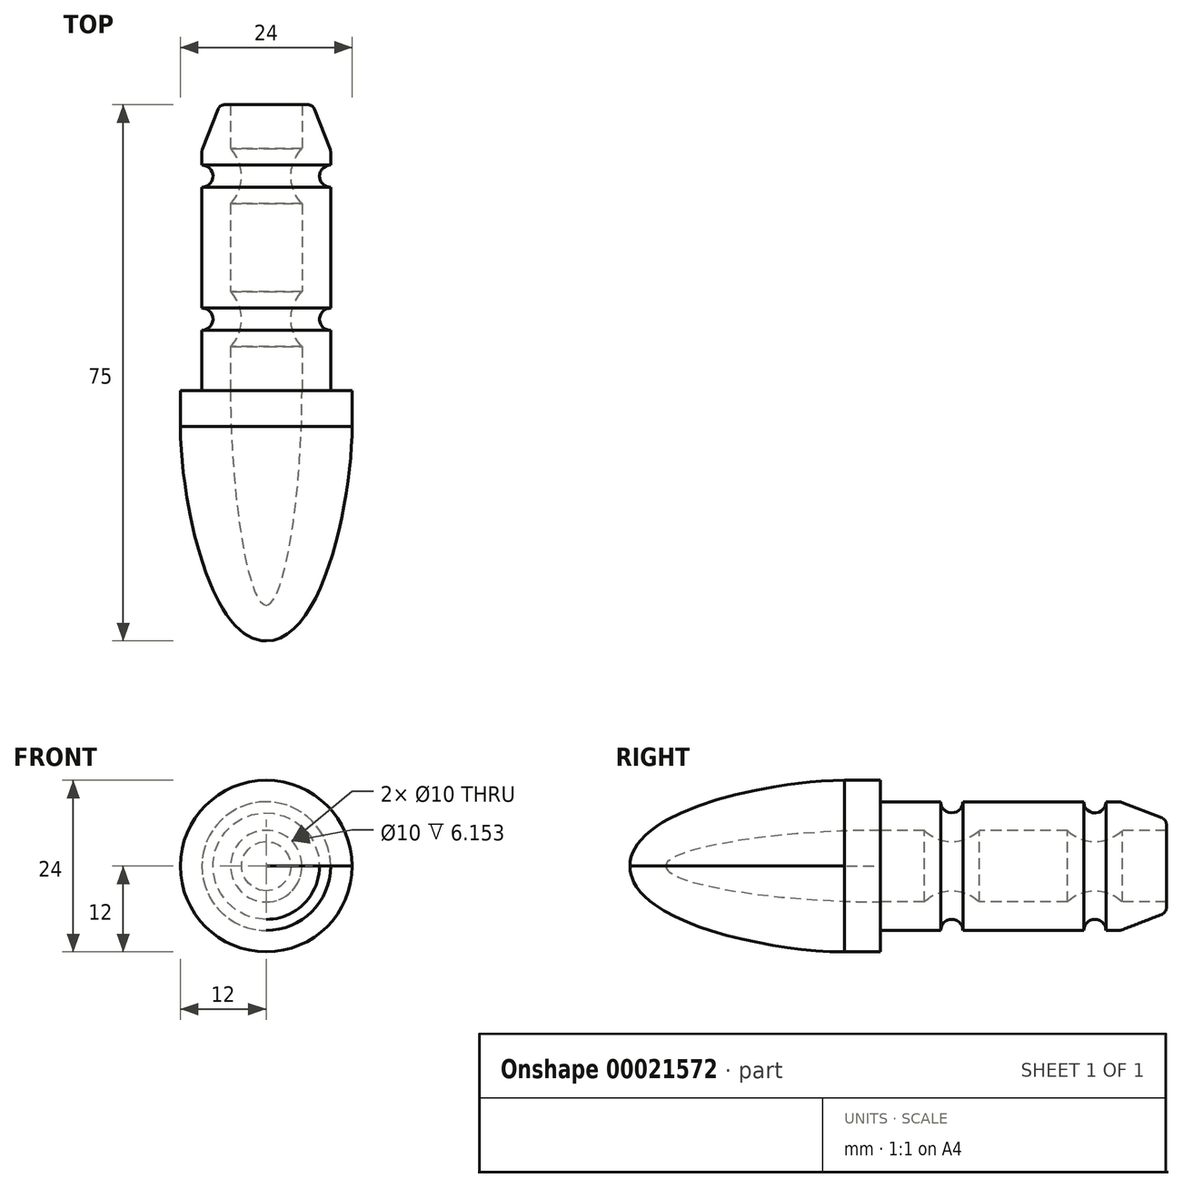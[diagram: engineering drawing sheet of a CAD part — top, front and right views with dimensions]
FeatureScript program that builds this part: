
annotation { "Feature Type Name" : "Feature", "Feature Type Description" : "" }
export const myFeature = defineFeature(function(context is Context, id is Id, definition is map)
    precondition{}
    {
        {
            var Q0;
            Q0=qCreatedBy(makeId("Top.planeOp"),FACE);
            var sketch = newSketch(context, id + "F0", { "sketchPlane" : qUnion([Q0])});
            skLineSegment(sketch, "E0", {"start": v(9, -6.45) * mm, "end": v(9, -8.45) * mm});
            skLineSegment(sketch, "E1", {"start": v(9.1, -40) * mm, "end": v(12, -40) * mm});
            skLineSegment(sketch, "E2", {"start": v(12, -40) * mm, "end": v(12, -45) * mm});
            skPoint(sketch, "E3", {"position": v(0, -75) * mm});
            skLineSegment(sketch, "E4", {"start": v(0, -75) * mm, "end": v(-13.94, -75) * mm, "construction": true});
            skFitSpline(sketch, "E5", {"points": [v(12, -45) * mm, v(0, -75) * mm], "startDerivative": vector(0, -30) * mm, "endDerivative": vector(-24, 0) * mm});
            skPoint(sketch, "E6.orphan", {"position": v(0, 0) * mm});
            skLineSegment(sketch, "E7", {"start": v(0, -55) * mm, "end": v(0, 0) * mm, "construction": true});
            skArc(sketch, "E8", {"start": v(9, -8.45) * mm, "mid": v(7.45, -10) * mm, "end": v(9, -11.55) * mm});
            skArc(sketch, "E9", {"start": v(9, -28.45) * mm, "mid": v(7.45, -30) * mm, "end": v(9, -31.55) * mm});
            skLineSegment(sketch, "E10.trimOffspring", {"start": v(9, -11.55) * mm, "end": v(9, -28.45) * mm});
            skLineSegment(sketch, "E11.trimOffspring", {"start": v(9, -31.55) * mm, "end": v(9, -39.9) * mm});
            skLineSegment(sketch, "E12.0", {"start": v(5, -33.85) * mm, "end": v(5, -40) * mm});
            skLineSegment(sketch, "E12.1", {"start": v(5, 0) * mm, "end": v(5, -6.15) * mm});
            skArc(sketch, "E12.2", {"start": v(5, -6.15) * mm, "mid": v(3.45, -10) * mm, "end": v(5, -13.85) * mm});
            skLineSegment(sketch, "E12.3", {"start": v(5, -13.85) * mm, "end": v(5, -26.15) * mm});
            skArc(sketch, "E12.4", {"start": v(5, -26.15) * mm, "mid": v(3.45, -30) * mm, "end": v(5, -33.85) * mm});
            skPoint(sketch, "E13", {"position": v(0, -70) * mm});
            skLineSegment(sketch, "E14", {"start": v(0, -70) * mm, "end": v(-16.95, -70) * mm, "construction": true});
            skFitSpline(sketch, "E15", {"points": [v(0, -70) * mm, v(5, -40) * mm], "startDerivative": vector(7.5, 0) * mm, "endDerivative": vector(0, 45) * mm});
            skLineSegment(sketch, "E16", {"start": v(6.5, 0) * mm, "end": v(5, 0) * mm});
            skPoint(sketch, "E17.visualSharp", {"position": v(9, 0) * mm});
            skPoint(sketch, "E18.visualSharp", {"position": v(9, -40) * mm});
            skArc(sketch, "E18.filletArc", {"start": v(9, -39.9) * mm, "mid": v(9.03, -39.97) * mm, "end": v(9.1, -40) * mm});
            skLineSegment(sketch, "E19", {"start": v(0, -70) * mm, "end": v(0, -75) * mm});
            skLineSegment(sketch, "E20", {"start": v(6.5, 0) * mm, "end": v(9, -6.45) * mm});
            skSolve(sketch);
        }
        {
            var Q0;
            Q0 = qSketchRegion(id + "F0", true);
            var Q1;
            Q1=sQuery(id+"F0.wireOp",EDGE,"E7");
            revolve(context, id + "F1", {"entities" : qUnion([Q0]), "axis" : qUnion([Q1]), "revolveType" : RevolveType.FULL});
        }
        {
            var Q0;
            Q0=makeQuery(id+"F1.opRevolve","SWEPT_EDGE",EDGE,{"disambiguationData":[OSD([sQuery(id+"F0.wireOp",EDGE,"E16"),sQuery(id+"F0.wireOp",EDGE,"E20")])]});
            var Q1;
            Q1=makeQuery(id+"F1.opRevolve","SWEPT_EDGE",EDGE,{"disambiguationData":[OSD([sQuery(id+"F0.wireOp",EDGE,"E0"),sQuery(id+"F0.wireOp",EDGE,"E20")])]});
            fillet(context, id + "F2", {"entities" : qUnion([Q0, Q1]), "radius" : 1 * mm, "tangentPropagation" : true, "allowEdgeOverflow" : false});
        }
    });
